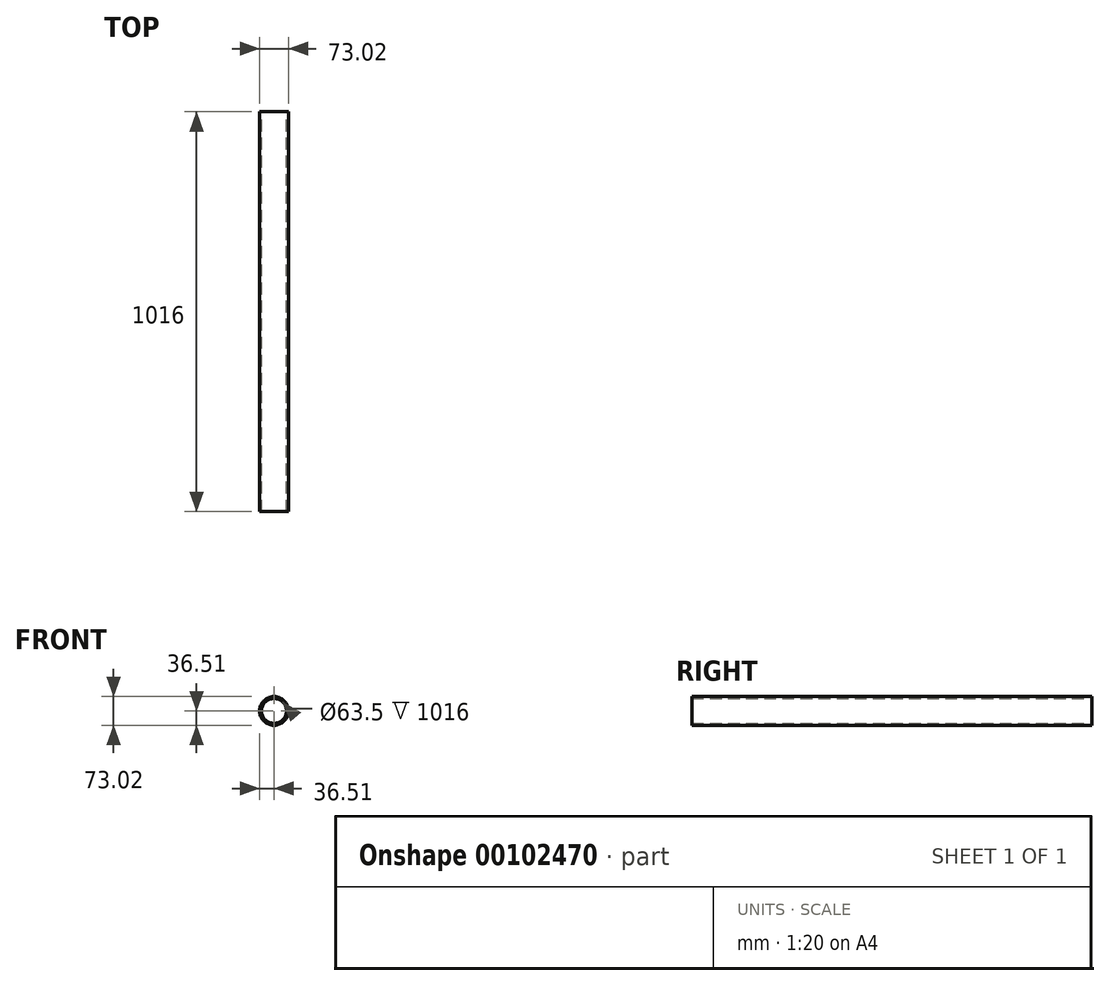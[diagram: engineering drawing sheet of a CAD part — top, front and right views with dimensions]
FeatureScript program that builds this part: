
annotation { "Feature Type Name" : "Feature", "Feature Type Description" : "" }
export const myFeature = defineFeature(function(context is Context, id is Id, definition is map)
    precondition{}
    {
        {
            var Q0;
            Q0=qCreatedBy(makeId("Front.planeOp"),FACE);
            var sketch = newSketch(context, id + "F0", { "sketchPlane" : qUnion([Q0])});
            skCircle(sketch, "E0", {"center": v(0, 0) * mm, "radius": 31.75 * mm});
            skCircle(sketch, "E1", {"center": v(0, 0) * mm, "radius": 36.51 * mm});
            skSolve(sketch);
        }
        {
            var Q0;
            Q0 = qSketchRegion(id + "F0", true);
            extrude(context, id + "F1", {"entities" : qUnion([Q0]), "depth" : 1016 * mm});
        }
    });
